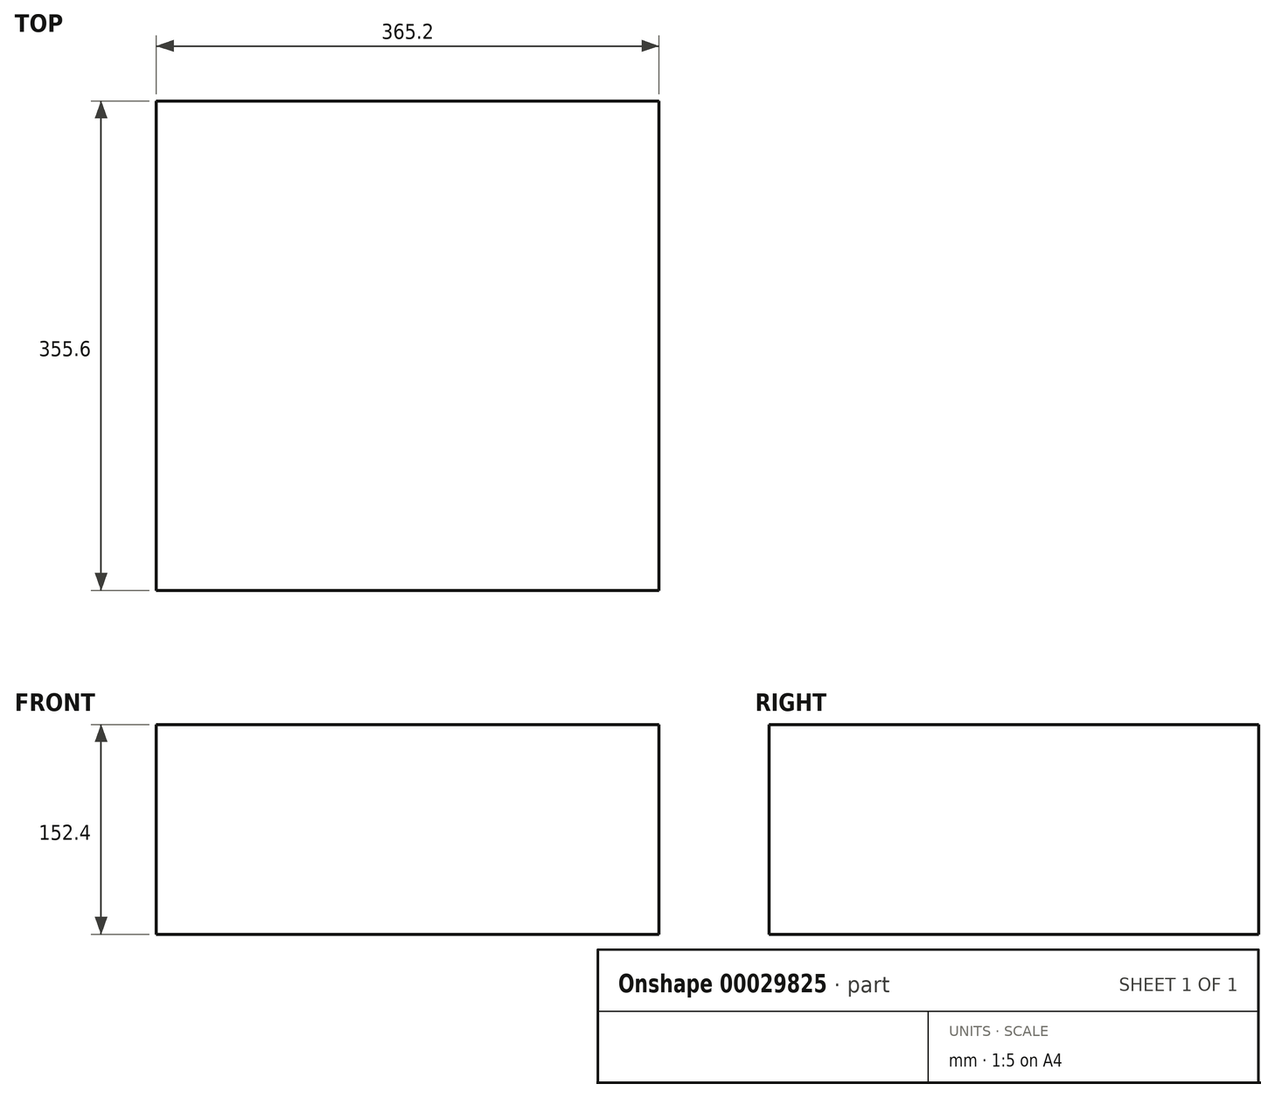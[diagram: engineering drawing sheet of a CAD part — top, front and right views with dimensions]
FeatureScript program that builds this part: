
annotation { "Feature Type Name" : "Feature", "Feature Type Description" : "" }
export const myFeature = defineFeature(function(context is Context, id is Id, definition is map)
    precondition{}
    {
        {
            var Q0;
            Q0=qCreatedBy(makeId("Top.planeOp"),FACE);
            var sketch = newSketch(context, id + "F0", { "sketchPlane" : qUnion([Q0])});
            skLineSegment(sketch, "E0.rect.bottom", {"start": v(-182.6, 177.8) * mm, "end": v(182.6, 177.8) * mm});
            skLineSegment(sketch, "E0.rect.top", {"start": v(-182.6, -177.8) * mm, "end": v(182.6, -177.8) * mm});
            skLineSegment(sketch, "E0.rect.left", {"start": v(-182.6, 177.8) * mm, "end": v(-182.6, -177.8) * mm});
            skLineSegment(sketch, "E0.rect.right", {"start": v(182.6, 177.8) * mm, "end": v(182.6, -177.8) * mm});
            skPoint(sketch, "E0.rect.middle", {"position": v(0, 0) * mm});
            skSolve(sketch);
        }
        {
            var Q0;
            Q0=qSketchRegion(id+"F0",true);
            extrude(context, id + "F1", {"entities" : qUnion([Q0]), "depth" : 152.4 * mm});
        }
    });
